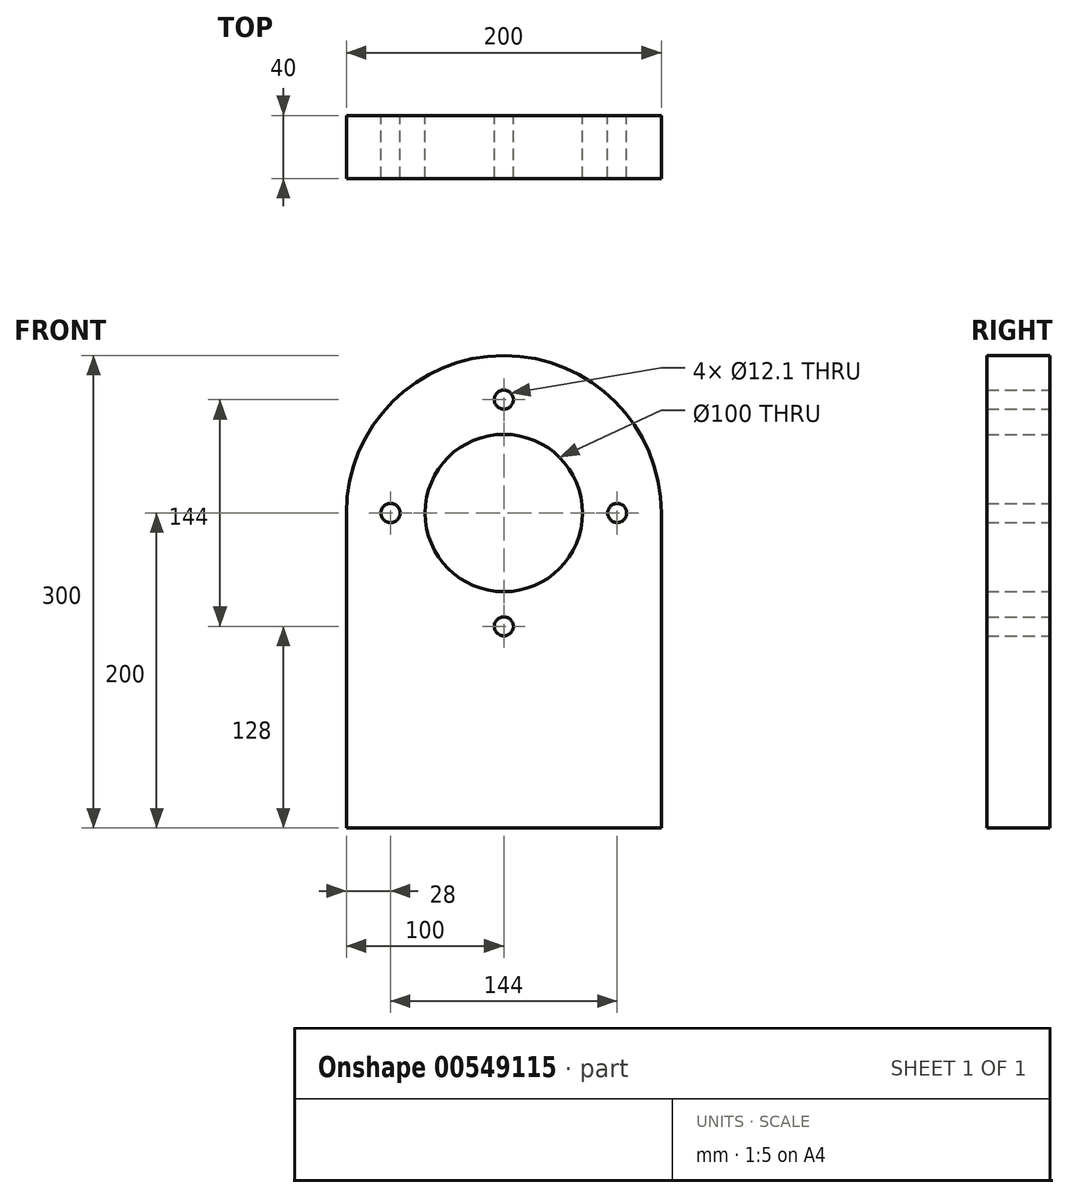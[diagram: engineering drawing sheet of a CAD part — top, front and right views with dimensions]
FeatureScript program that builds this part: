
annotation { "Feature Type Name" : "Feature", "Feature Type Description" : "" }
export const myFeature = defineFeature(function(context is Context, id is Id, definition is map)
    precondition{}
    {
        {
            var Q0;
            Q0=qCreatedBy(makeId("Front.planeOp"),FACE);
            var sketch = newSketch(context, id + "F0", { "sketchPlane" : qUnion([Q0])});
            skLineSegment(sketch, "E0.bottom", {"start": v(-100, 0) * mm, "end": v(100, 0) * mm});
            skLineSegment(sketch, "E0.left", {"start": v(-100, 0) * mm, "end": v(-100, 200) * mm});
            skLineSegment(sketch, "E0.right", {"start": v(100, 0) * mm, "end": v(100, 200) * mm});
            skArc(sketch, "E1", {"start": v(100, 200) * mm, "mid": v(0, 300) * mm, "end": v(-100, 200) * mm});
            skCircle(sketch, "E2", {"center": v(0, 200) * mm, "radius": 50 * mm});
            skCircle(sketch, "E3", {"center": v(0, 200) * mm, "radius": 72 * mm, "construction": true});
            skPoint(sketch, "E4", {"position": v(0, 272) * mm});
            skPoint(sketch, "E5.1.0", {"position": v(-72, 200) * mm});
            skPoint(sketch, "E5.2.0", {"position": v(0, 128) * mm});
            skPoint(sketch, "E6.0.3.0", {"position": v(72, 200) * mm});
            skLineSegment(sketch, "E7", {"start": v(-100, 40) * mm, "end": v(100, 40) * mm});
            skSolve(sketch);
        }
        {
            var Q0;
            Q0 = qSketchRegion(id + "F0", true);
            extrude(context, id + "F1", {"entities" : qUnion([Q0]), "depth" : 40 * mm, "offsetDistance" : 25 * mm});
        }
        {
            var Q0;
            Q0=sQuery(id+"F0.wireOp",VERTEX,"E4");
            var Q1;
            Q1=sQuery(id+"F0.wireOp",VERTEX,"E5.1.0");
            var Q2;
            Q2=sQuery(id+"F0.wireOp",VERTEX,"E5.2.0");
            var Q3;
            Q3=sQuery(id+"F0.wireOp",VERTEX,"E6.0.3.0");
            var Q4;
            Q4=makeQuery(id+"F1.opExtrude","SWEPT_BODY",BODY,{"disambiguationData":[OSD([sQuery(id+"F0.wireOp",EDGE,"E0.bottom"),sQuery(id+"F0.wireOp",EDGE,"E0.left"),sQuery(id+"F0.wireOp",EDGE,"E0.right"),sQuery(id+"F0.wireOp",EDGE,"E1"),sQuery(id+"F0.wireOp",EDGE,"E2")])]});
            hole(context, id + "F2", {"style" : HoleStyle.SIMPLE, "endStyle" : HoleEndStyle.THROUGH, "oppositeDirection" : true, "standardTappedOrClearance" : lookupTablePath({ "standard" : "ISO", "engagement" : "75%", "pitch" : "2 mm", "size" : "M14", "type" : "Tapped" }), "standardBlindInLast" : lookupTablePath({ "standard" : "ISO", "engagement" : "75%", "pitch" : "2 mm", "size" : "M14", "type" : "Tapped" }), "holeDiameter" : 12.1 * mm, "showTappedDepth" : true, "tappedDepth" : 12 * mm, "tapClearance" : 3, "locations" : qUnion([Q0, Q1, Q2, Q3]), "scope" : qUnion([Q4]), "majorDiameter" : 14 * mm});
        }
    });
